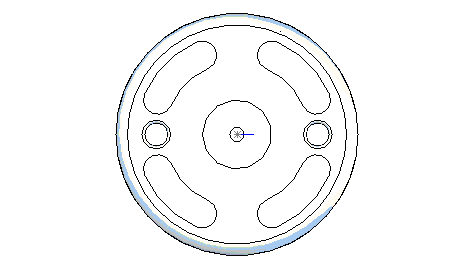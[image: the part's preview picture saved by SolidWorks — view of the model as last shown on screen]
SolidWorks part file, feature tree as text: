
SOLIDWORKS PART (.sldprt)
format: sldprt  version: not decoded by parser v0  size: 282,624 bytes
history: native  units: mm
features: material x9, fillet x3, cut_extrude x2, plane x1, sketch x1, revolve x1, pattern_circular x1 + 5 further entries (+14 scaffold rows collapsed)
feature tree (37):
  scaffold x14  (default folders/planes/origin — collapsed)
  material  "Matériau <non spécifié>"
  material  "param"
  material  "param"
  material  "param"
  material  "param"
  material  "param"
  material  "param"
  material  "param"
  material  "param"
  "Corps de surface"
  plane  "Face"
  "Dessus"
  "Droite"
  sketch  "Esquisse1"
  revolve  "Révolution1"  Angle=360deg
  fillet  "Congé1"  Radius=2mm
  fillet  "Congé2"  Radius=1mm
  "Esquisse2"
  cut_extrude  "Enlèv. mat.-Extru.1"  [1 undecoded]
  fillet  "Congé3"  Radius=0.5mm
  "Esquisse3"
  cut_extrude  "Enlèv. mat.-Extru.2"  Depth=100mm
  pattern_circular  "Répétition circulaire1"  Count=2 Angle=90deg
decode coverage: 6 of 8 modeling features carry decoded parameters; 5 rows unclassified (native names shown)
note: 1 parameter value undecoded
note: suppression state not decoded; provenance and decode notes live in map.json
